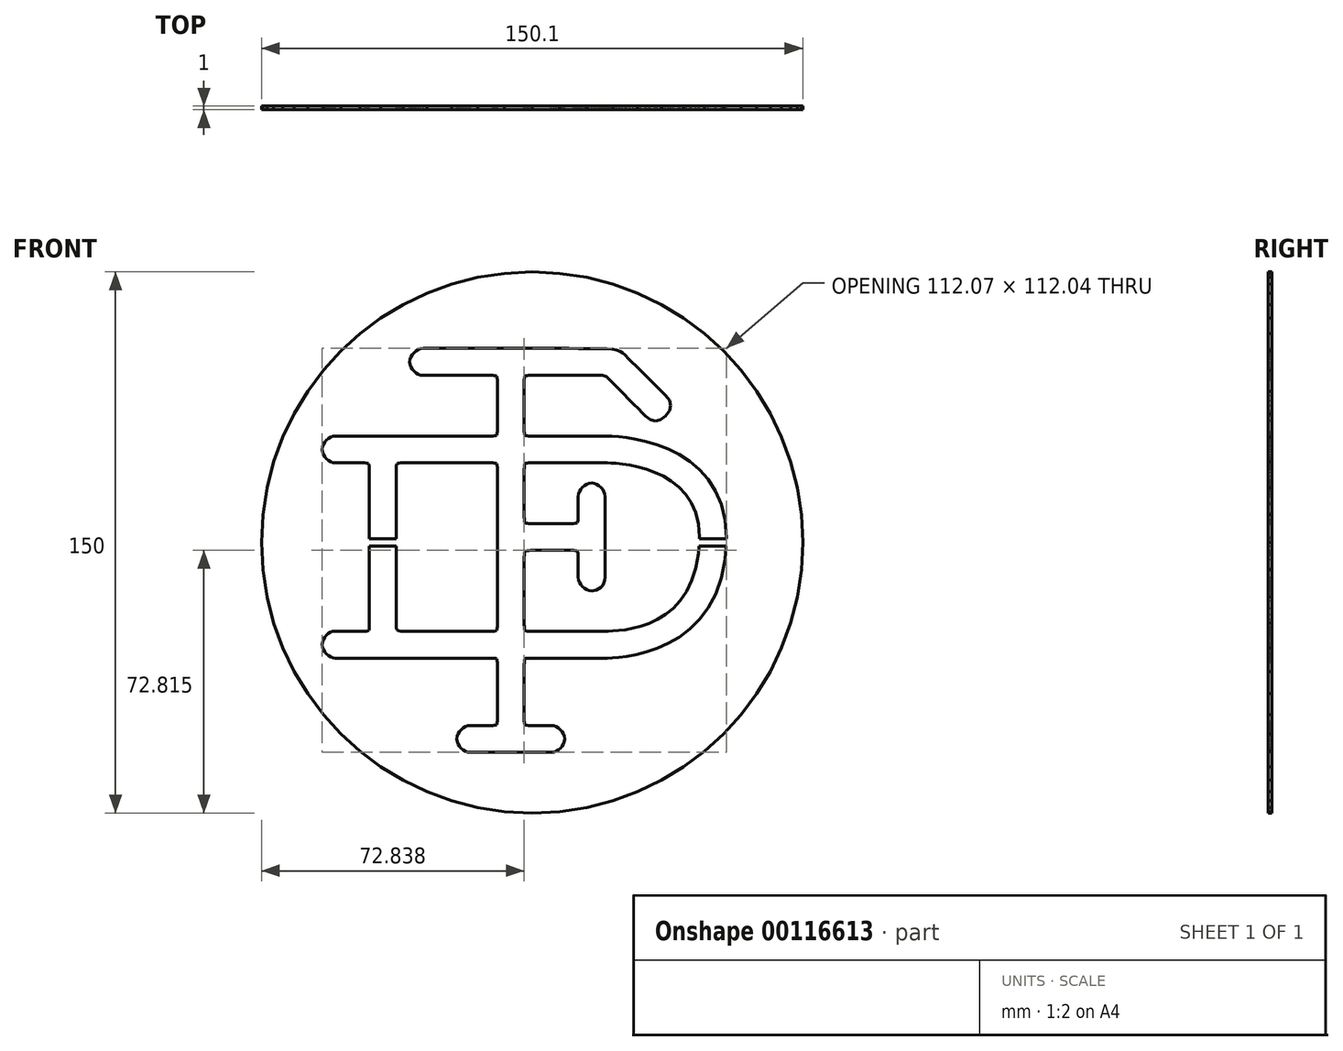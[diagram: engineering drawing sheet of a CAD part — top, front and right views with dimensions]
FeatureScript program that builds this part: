
annotation { "Feature Type Name" : "Feature", "Feature Type Description" : "" }
export const myFeature = defineFeature(function(context is Context, id is Id, definition is map)
    precondition{}
    {
        {
            var Q0;
            Q0=qCreatedBy(makeId("Front.planeOp"),FACE);
            var sketch = newSketch(context, id + "F0", { "sketchPlane" : qUnion([Q0])});
            skLineSegment(sketch, "E0", {"start": v(-30.25, 46.32) * mm, "end": v(-30.95, 46.4) * mm});
            skLineSegment(sketch, "E1", {"start": v(-30.95, 46.4) * mm, "end": v(-31.62, 46.64) * mm});
            skLineSegment(sketch, "E2", {"start": v(-31.62, 46.64) * mm, "end": v(-32.25, 47) * mm});
            skLineSegment(sketch, "E3", {"start": v(-32.25, 47) * mm, "end": v(-32.81, 47.49) * mm});
            skLineSegment(sketch, "E4", {"start": v(-32.81, 47.49) * mm, "end": v(-33.28, 48.05) * mm});
            skLineSegment(sketch, "E5", {"start": v(-33.28, 48.05) * mm, "end": v(-33.65, 48.68) * mm});
            skLineSegment(sketch, "E6", {"start": v(-33.65, 48.68) * mm, "end": v(-33.88, 49.35) * mm});
            skLineSegment(sketch, "E7", {"start": v(-33.88, 49.35) * mm, "end": v(-33.97, 50.05) * mm});
            skLineSegment(sketch, "E8", {"start": v(-33.97, 50.05) * mm, "end": v(-33.88, 50.75) * mm});
            skLineSegment(sketch, "E9", {"start": v(-33.88, 50.75) * mm, "end": v(-33.65, 51.43) * mm});
            skLineSegment(sketch, "E10", {"start": v(-33.65, 51.43) * mm, "end": v(-33.28, 52.07) * mm});
            skLineSegment(sketch, "E11", {"start": v(-33.28, 52.07) * mm, "end": v(-32.81, 52.64) * mm});
            skLineSegment(sketch, "E12", {"start": v(-32.81, 52.64) * mm, "end": v(-32.25, 53.13) * mm});
            skLineSegment(sketch, "E13", {"start": v(-32.25, 53.13) * mm, "end": v(-31.62, 53.5) * mm});
            skLineSegment(sketch, "E14", {"start": v(-31.62, 53.5) * mm, "end": v(-30.95, 53.75) * mm});
            skLineSegment(sketch, "E15", {"start": v(-30.95, 53.75) * mm, "end": v(-30.25, 53.84) * mm});
            skLineSegment(sketch, "E16", {"start": v(-30.25, 53.84) * mm, "end": v(-29.61, 53.84) * mm});
            skLineSegment(sketch, "E17", {"start": v(-29.61, 53.84) * mm, "end": v(-28.42, 53.83) * mm});
            skLineSegment(sketch, "E18", {"start": v(-28.42, 53.83) * mm, "end": v(-26.74, 53.83) * mm});
            skLineSegment(sketch, "E19", {"start": v(-26.74, 53.83) * mm, "end": v(-24.63, 53.83) * mm});
            skLineSegment(sketch, "E20", {"start": v(-24.63, 53.83) * mm, "end": v(-22.15, 53.82) * mm});
            skLineSegment(sketch, "E21", {"start": v(-22.15, 53.82) * mm, "end": v(-19.35, 53.82) * mm});
            skLineSegment(sketch, "E22", {"start": v(-19.35, 53.82) * mm, "end": v(-16.3, 53.82) * mm});
            skLineSegment(sketch, "E23", {"start": v(-16.3, 53.82) * mm, "end": v(-13.05, 53.81) * mm});
            skLineSegment(sketch, "E24", {"start": v(-13.05, 53.81) * mm, "end": v(-9.67, 53.8) * mm});
            skLineSegment(sketch, "E25", {"start": v(-9.67, 53.8) * mm, "end": v(-6.2, 53.8) * mm});
            skLineSegment(sketch, "E26", {"start": v(-6.2, 53.8) * mm, "end": v(-2.73, 53.8) * mm});
            skLineSegment(sketch, "E27", {"start": v(-2.73, 53.8) * mm, "end": v(0.71, 53.8) * mm});
            skLineSegment(sketch, "E28", {"start": v(0.71, 53.8) * mm, "end": v(4.05, 53.8) * mm});
            skLineSegment(sketch, "E29", {"start": v(4.05, 53.8) * mm, "end": v(7.24, 53.79) * mm});
            skLineSegment(sketch, "E30", {"start": v(7.24, 53.79) * mm, "end": v(10.2, 53.79) * mm});
            skLineSegment(sketch, "E31", {"start": v(10.2, 53.79) * mm, "end": v(12.9, 53.79) * mm});
            skLineSegment(sketch, "E32", {"start": v(12.9, 53.79) * mm, "end": v(16.15, 53.78) * mm});
            skLineSegment(sketch, "E33", {"start": v(16.15, 53.78) * mm, "end": v(18.72, 53.76) * mm});
            skLineSegment(sketch, "E34", {"start": v(18.72, 53.76) * mm, "end": v(20.72, 53.7) * mm});
            skLineSegment(sketch, "E35", {"start": v(20.72, 53.7) * mm, "end": v(22.25, 53.57) * mm});
            skLineSegment(sketch, "E36", {"start": v(22.25, 53.57) * mm, "end": v(23.42, 53.35) * mm});
            skLineSegment(sketch, "E37", {"start": v(23.42, 53.35) * mm, "end": v(24.34, 53.01) * mm});
            skLineSegment(sketch, "E38", {"start": v(24.34, 53.01) * mm, "end": v(25.1, 52.55) * mm});
            skLineSegment(sketch, "E39", {"start": v(25.1, 52.55) * mm, "end": v(25.8, 51.92) * mm});
            skLineSegment(sketch, "E40", {"start": v(25.8, 51.92) * mm, "end": v(26.74, 50.98) * mm});
            skLineSegment(sketch, "E41", {"start": v(26.74, 50.98) * mm, "end": v(28.08, 49.64) * mm});
            skLineSegment(sketch, "E42", {"start": v(28.08, 49.64) * mm, "end": v(29.68, 48.05) * mm});
            skLineSegment(sketch, "E43", {"start": v(29.68, 48.05) * mm, "end": v(31.4, 46.32) * mm});
            skLineSegment(sketch, "E44", {"start": v(31.4, 46.32) * mm, "end": v(33.14, 44.6) * mm});
            skLineSegment(sketch, "E45", {"start": v(33.14, 44.6) * mm, "end": v(34.73, 43) * mm});
            skLineSegment(sketch, "E46", {"start": v(34.73, 43) * mm, "end": v(36.07, 41.66) * mm});
            skLineSegment(sketch, "E47", {"start": v(36.07, 41.66) * mm, "end": v(37, 40.72) * mm});
            skLineSegment(sketch, "E48", {"start": v(37, 40.72) * mm, "end": v(38.06, 39.32) * mm});
            skLineSegment(sketch, "E49", {"start": v(38.06, 39.32) * mm, "end": v(38.41, 37.92) * mm});
            skLineSegment(sketch, "E50", {"start": v(38.41, 37.92) * mm, "end": v(38.06, 36.52) * mm});
            skLineSegment(sketch, "E51", {"start": v(38.06, 36.52) * mm, "end": v(37, 35.12) * mm});
            skLineSegment(sketch, "E52", {"start": v(37, 35.12) * mm, "end": v(35.6, 34.07) * mm});
            skLineSegment(sketch, "E53", {"start": v(35.6, 34.07) * mm, "end": v(34.2, 33.72) * mm});
            skLineSegment(sketch, "E54", {"start": v(34.2, 33.72) * mm, "end": v(32.8, 34.07) * mm});
            skLineSegment(sketch, "E55", {"start": v(32.8, 34.07) * mm, "end": v(31.4, 35.12) * mm});
            skLineSegment(sketch, "E56", {"start": v(31.4, 35.12) * mm, "end": v(30.55, 35.98) * mm});
            skLineSegment(sketch, "E57", {"start": v(30.55, 35.98) * mm, "end": v(29.42, 37.11) * mm});
            skLineSegment(sketch, "E58", {"start": v(29.42, 37.11) * mm, "end": v(28.13, 38.42) * mm});
            skLineSegment(sketch, "E59", {"start": v(28.13, 38.42) * mm, "end": v(26.74, 39.81) * mm});
            skLineSegment(sketch, "E60", {"start": v(26.74, 39.81) * mm, "end": v(25.35, 41.2) * mm});
            skLineSegment(sketch, "E61", {"start": v(25.35, 41.2) * mm, "end": v(24.05, 42.51) * mm});
            skLineSegment(sketch, "E62", {"start": v(24.05, 42.51) * mm, "end": v(22.93, 43.64) * mm});
            skLineSegment(sketch, "E63", {"start": v(22.93, 43.64) * mm, "end": v(22.07, 44.5) * mm});
            skLineSegment(sketch, "E64", {"start": v(22.07, 44.5) * mm, "end": v(21.45, 45.12) * mm});
            skLineSegment(sketch, "E65", {"start": v(21.45, 45.12) * mm, "end": v(20.96, 45.58) * mm});
            skLineSegment(sketch, "E66", {"start": v(20.96, 45.58) * mm, "end": v(20.56, 45.92) * mm});
            skLineSegment(sketch, "E67", {"start": v(20.56, 45.92) * mm, "end": v(20.2, 46.14) * mm});
            skLineSegment(sketch, "E68", {"start": v(20.2, 46.14) * mm, "end": v(19.84, 46.28) * mm});
            skLineSegment(sketch, "E69", {"start": v(19.84, 46.28) * mm, "end": v(19.43, 46.34) * mm});
            skLineSegment(sketch, "E70", {"start": v(19.43, 46.34) * mm, "end": v(18.94, 46.37) * mm});
            skLineSegment(sketch, "E71", {"start": v(18.94, 46.37) * mm, "end": v(18.3, 46.37) * mm});
            skLineSegment(sketch, "E72", {"start": v(18.3, 46.37) * mm, "end": v(17.02, 46.37) * mm});
            skLineSegment(sketch, "E73", {"start": v(17.02, 46.37) * mm, "end": v(14.8, 46.37) * mm});
            skLineSegment(sketch, "E74", {"start": v(14.8, 46.37) * mm, "end": v(11.95, 46.36) * mm});
            skLineSegment(sketch, "E75", {"start": v(11.95, 46.36) * mm, "end": v(8.8, 46.35) * mm});
            skLineSegment(sketch, "E76", {"start": v(8.8, 46.35) * mm, "end": v(5.66, 46.34) * mm});
            skLineSegment(sketch, "E77", {"start": v(5.66, 46.34) * mm, "end": v(2.88, 46.33) * mm});
            skLineSegment(sketch, "E78", {"start": v(2.88, 46.33) * mm, "end": v(0.76, 46.32) * mm});
            skLineSegment(sketch, "E79", {"start": v(0.76, 46.32) * mm, "end": v(-0.37, 46.32) * mm});
            skLineSegment(sketch, "E80", {"start": v(-0.37, 46.32) * mm, "end": v(-0.98, 46.32) * mm});
            skLineSegment(sketch, "E81", {"start": v(-0.98, 46.32) * mm, "end": v(-1.44, 46.3) * mm});
            skLineSegment(sketch, "E82", {"start": v(-1.44, 46.3) * mm, "end": v(-1.76, 46.22) * mm});
            skLineSegment(sketch, "E83", {"start": v(-1.76, 46.22) * mm, "end": v(-1.98, 46.09) * mm});
            skLineSegment(sketch, "E84", {"start": v(-1.98, 46.09) * mm, "end": v(-2.12, 45.87) * mm});
            skLineSegment(sketch, "E85", {"start": v(-2.12, 45.87) * mm, "end": v(-2.18, 45.54) * mm});
            skLineSegment(sketch, "E86", {"start": v(-2.18, 45.54) * mm, "end": v(-2.2, 45.09) * mm});
            skLineSegment(sketch, "E87", {"start": v(-2.2, 45.09) * mm, "end": v(-2.21, 44.48) * mm});
            skLineSegment(sketch, "E88", {"start": v(-2.21, 44.48) * mm, "end": v(-2.21, 43.46) * mm});
            skLineSegment(sketch, "E89", {"start": v(-2.21, 43.46) * mm, "end": v(-2.21, 41.91) * mm});
            skLineSegment(sketch, "E90", {"start": v(-2.21, 41.91) * mm, "end": v(-2.21, 40.02) * mm});
            skLineSegment(sketch, "E91", {"start": v(-2.21, 40.02) * mm, "end": v(-2.21, 37.94) * mm});
            skLineSegment(sketch, "E92", {"start": v(-2.21, 37.94) * mm, "end": v(-2.21, 35.87) * mm});
            skLineSegment(sketch, "E93", {"start": v(-2.21, 35.87) * mm, "end": v(-2.21, 33.98) * mm});
            skLineSegment(sketch, "E94", {"start": v(-2.21, 33.98) * mm, "end": v(-2.21, 32.43) * mm});
            skLineSegment(sketch, "E95", {"start": v(-2.21, 32.43) * mm, "end": v(-2.21, 31.41) * mm});
            skLineSegment(sketch, "E96", {"start": v(-2.21, 31.41) * mm, "end": v(-2.2, 30.79) * mm});
            skLineSegment(sketch, "E97", {"start": v(-2.2, 30.79) * mm, "end": v(-2.18, 30.32) * mm});
            skLineSegment(sketch, "E98", {"start": v(-2.18, 30.32) * mm, "end": v(-2.12, 29.98) * mm});
            skLineSegment(sketch, "E99", {"start": v(-2.12, 29.98) * mm, "end": v(-1.98, 29.76) * mm});
            skLineSegment(sketch, "E100", {"start": v(-1.98, 29.76) * mm, "end": v(-1.76, 29.62) * mm});
            skLineSegment(sketch, "E101", {"start": v(-1.76, 29.62) * mm, "end": v(-1.44, 29.55) * mm});
            skLineSegment(sketch, "E102", {"start": v(-1.44, 29.55) * mm, "end": v(-0.98, 29.52) * mm});
            skLineSegment(sketch, "E103", {"start": v(-0.98, 29.52) * mm, "end": v(-0.37, 29.52) * mm});
            skLineSegment(sketch, "E104", {"start": v(-0.37, 29.52) * mm, "end": v(0.97, 29.52) * mm});
            skLineSegment(sketch, "E105", {"start": v(0.97, 29.52) * mm, "end": v(3.37, 29.52) * mm});
            skLineSegment(sketch, "E106", {"start": v(3.37, 29.52) * mm, "end": v(6.46, 29.52) * mm});
            skLineSegment(sketch, "E107", {"start": v(6.46, 29.52) * mm, "end": v(9.9, 29.52) * mm});
            skLineSegment(sketch, "E108", {"start": v(9.9, 29.52) * mm, "end": v(13.35, 29.52) * mm});
            skLineSegment(sketch, "E109", {"start": v(13.35, 29.52) * mm, "end": v(16.45, 29.52) * mm});
            skLineSegment(sketch, "E110", {"start": v(16.45, 29.52) * mm, "end": v(18.85, 29.52) * mm});
            skLineSegment(sketch, "E111", {"start": v(18.85, 29.52) * mm, "end": v(20.2, 29.52) * mm});
            skLineSegment(sketch, "E112", {"start": v(20.2, 29.52) * mm, "end": v(20.88, 29.5) * mm});
            skLineSegment(sketch, "E113", {"start": v(20.88, 29.5) * mm, "end": v(22.17, 29.45) * mm});
            skLineSegment(sketch, "E114", {"start": v(22.17, 29.45) * mm, "end": v(23.99, 29.31) * mm});
            skLineSegment(sketch, "E115", {"start": v(23.99, 29.31) * mm, "end": v(26.23, 29.04) * mm});
            skLineSegment(sketch, "E116", {"start": v(26.23, 29.04) * mm, "end": v(28.8, 28.6) * mm});
            skLineSegment(sketch, "E117", {"start": v(28.8, 28.6) * mm, "end": v(31.64, 27.96) * mm});
            skLineSegment(sketch, "E118", {"start": v(31.64, 27.96) * mm, "end": v(34.63, 27.07) * mm});
            skLineSegment(sketch, "E119", {"start": v(34.63, 27.07) * mm, "end": v(37.7, 25.9) * mm});
            skLineSegment(sketch, "E120", {"start": v(37.7, 25.9) * mm, "end": v(40.73, 24.39) * mm});
            skLineSegment(sketch, "E121", {"start": v(40.73, 24.39) * mm, "end": v(43.66, 22.51) * mm});
            skLineSegment(sketch, "E122", {"start": v(43.66, 22.51) * mm, "end": v(46.38, 20.23) * mm});
            skLineSegment(sketch, "E123", {"start": v(46.38, 20.23) * mm, "end": v(48.81, 17.5) * mm});
            skLineSegment(sketch, "E124", {"start": v(48.81, 17.5) * mm, "end": v(50.87, 14.27) * mm});
            skLineSegment(sketch, "E125", {"start": v(50.87, 14.27) * mm, "end": v(52.44, 10.52) * mm});
            skLineSegment(sketch, "E126", {"start": v(52.44, 10.52) * mm, "end": v(53.46, 6.2) * mm});
            skLineSegment(sketch, "E127", {"start": v(53.46, 6.2) * mm, "end": v(53.82, 1.27) * mm});
            skLineSegment(sketch, "E128", {"start": v(53.82, 1.27) * mm, "end": v(53.47, -4.64) * mm});
            skLineSegment(sketch, "E129", {"start": v(53.47, -4.64) * mm, "end": v(52.46, -9.8) * mm});
            skLineSegment(sketch, "E130", {"start": v(52.46, -9.8) * mm, "end": v(50.89, -14.28) * mm});
            skLineSegment(sketch, "E131", {"start": v(50.89, -14.28) * mm, "end": v(48.84, -18.11) * mm});
            skLineSegment(sketch, "E132", {"start": v(48.84, -18.11) * mm, "end": v(46.41, -21.35) * mm});
            skLineSegment(sketch, "E133", {"start": v(46.41, -21.35) * mm, "end": v(43.68, -24.04) * mm});
            skLineSegment(sketch, "E134", {"start": v(43.68, -24.04) * mm, "end": v(40.76, -26.24) * mm});
            skLineSegment(sketch, "E135", {"start": v(40.76, -26.24) * mm, "end": v(37.72, -28) * mm});
            skLineSegment(sketch, "E136", {"start": v(37.72, -28) * mm, "end": v(34.65, -29.36) * mm});
            skLineSegment(sketch, "E137", {"start": v(34.65, -29.36) * mm, "end": v(31.66, -30.38) * mm});
            skLineSegment(sketch, "E138", {"start": v(31.66, -30.38) * mm, "end": v(28.82, -31.1) * mm});
            skLineSegment(sketch, "E139", {"start": v(28.82, -31.1) * mm, "end": v(26.24, -31.59) * mm});
            skLineSegment(sketch, "E140", {"start": v(26.24, -31.59) * mm, "end": v(24, -31.87) * mm});
            skLineSegment(sketch, "E141", {"start": v(24, -31.87) * mm, "end": v(22.18, -32.02) * mm});
            skLineSegment(sketch, "E142", {"start": v(22.18, -32.02) * mm, "end": v(20.88, -32.07) * mm});
            skLineSegment(sketch, "E143", {"start": v(20.88, -32.07) * mm, "end": v(20.2, -32.07) * mm});
            skLineSegment(sketch, "E144", {"start": v(20.2, -32.07) * mm, "end": v(18.64, -32.07) * mm});
            skLineSegment(sketch, "E145", {"start": v(18.64, -32.07) * mm, "end": v(16.14, -32.07) * mm});
            skLineSegment(sketch, "E146", {"start": v(16.14, -32.07) * mm, "end": v(13.02, -32.07) * mm});
            skLineSegment(sketch, "E147", {"start": v(13.02, -32.07) * mm, "end": v(9.62, -32.07) * mm});
            skLineSegment(sketch, "E148", {"start": v(9.62, -32.07) * mm, "end": v(6.26, -32.07) * mm});
            skLineSegment(sketch, "E149", {"start": v(6.26, -32.07) * mm, "end": v(3.26, -32.07) * mm});
            skLineSegment(sketch, "E150", {"start": v(3.26, -32.07) * mm, "end": v(0.94, -32.07) * mm});
            skLineSegment(sketch, "E151", {"start": v(0.94, -32.07) * mm, "end": v(-0.38, -32.07) * mm});
            skLineSegment(sketch, "E152", {"start": v(-0.38, -32.07) * mm, "end": v(-0.98, -32.07) * mm});
            skLineSegment(sketch, "E153", {"start": v(-0.98, -32.07) * mm, "end": v(-1.44, -32.1) * mm});
            skLineSegment(sketch, "E154", {"start": v(-1.44, -32.1) * mm, "end": v(-1.76, -32.16) * mm});
            skLineSegment(sketch, "E155", {"start": v(-1.76, -32.16) * mm, "end": v(-1.98, -32.3) * mm});
            skLineSegment(sketch, "E156", {"start": v(-1.98, -32.3) * mm, "end": v(-2.11, -32.5) * mm});
            skLineSegment(sketch, "E157", {"start": v(-2.11, -32.5) * mm, "end": v(-2.18, -32.84) * mm});
            skLineSegment(sketch, "E158", {"start": v(-2.18, -32.84) * mm, "end": v(-2.2, -33.3) * mm});
            skLineSegment(sketch, "E159", {"start": v(-2.2, -33.3) * mm, "end": v(-2.21, -33.91) * mm});
            skLineSegment(sketch, "E160", {"start": v(-2.21, -33.91) * mm, "end": v(-2.21, -35.04) * mm});
            skLineSegment(sketch, "E161", {"start": v(-2.21, -35.04) * mm, "end": v(-2.21, -36.88) * mm});
            skLineSegment(sketch, "E162", {"start": v(-2.21, -36.88) * mm, "end": v(-2.21, -39.17) * mm});
            skLineSegment(sketch, "E163", {"start": v(-2.21, -39.17) * mm, "end": v(-2.21, -41.66) * mm});
            skLineSegment(sketch, "E164", {"start": v(-2.21, -41.66) * mm, "end": v(-2.21, -44.13) * mm});
            skLineSegment(sketch, "E165", {"start": v(-2.21, -44.13) * mm, "end": v(-2.21, -46.3) * mm});
            skLineSegment(sketch, "E166", {"start": v(-2.21, -46.3) * mm, "end": v(-2.21, -47.96) * mm});
            skLineSegment(sketch, "E167", {"start": v(-2.21, -47.96) * mm, "end": v(-2.21, -48.84) * mm});
            skLineSegment(sketch, "E168", {"start": v(-2.21, -48.84) * mm, "end": v(-2.2, -49.47) * mm});
            skLineSegment(sketch, "E169", {"start": v(-2.2, -49.47) * mm, "end": v(-2.19, -49.94) * mm});
            skLineSegment(sketch, "E170", {"start": v(-2.19, -49.94) * mm, "end": v(-2.12, -50.27) * mm});
            skLineSegment(sketch, "E171", {"start": v(-2.12, -50.27) * mm, "end": v(-2, -50.5) * mm});
            skLineSegment(sketch, "E172", {"start": v(-2, -50.5) * mm, "end": v(-1.78, -50.64) * mm});
            skLineSegment(sketch, "E173", {"start": v(-1.78, -50.64) * mm, "end": v(-1.45, -50.7) * mm});
            skLineSegment(sketch, "E174", {"start": v(-1.45, -50.7) * mm, "end": v(-1, -50.73) * mm});
            skLineSegment(sketch, "E175", {"start": v(-1, -50.73) * mm, "end": v(-0.38, -50.74) * mm});
            skLineSegment(sketch, "E176", {"start": v(-0.38, -50.74) * mm, "end": v(5.23, -50.74) * mm});
            skLineSegment(sketch, "E177", {"start": v(5.23, -50.74) * mm, "end": v(5.93, -50.82) * mm});
            skLineSegment(sketch, "E178", {"start": v(5.93, -50.82) * mm, "end": v(6.6, -51.06) * mm});
            skLineSegment(sketch, "E179", {"start": v(6.6, -51.06) * mm, "end": v(7.24, -51.43) * mm});
            skLineSegment(sketch, "E180", {"start": v(7.24, -51.43) * mm, "end": v(7.81, -51.9) * mm});
            skLineSegment(sketch, "E181", {"start": v(7.81, -51.9) * mm, "end": v(8.3, -52.47) * mm});
            skLineSegment(sketch, "E182", {"start": v(8.3, -52.47) * mm, "end": v(8.67, -53.1) * mm});
            skLineSegment(sketch, "E183", {"start": v(8.67, -53.1) * mm, "end": v(8.9, -53.77) * mm});
            skLineSegment(sketch, "E184", {"start": v(8.9, -53.77) * mm, "end": v(9, -54.47) * mm});
            skLineSegment(sketch, "E185", {"start": v(9, -54.47) * mm, "end": v(8.9, -55.17) * mm});
            skLineSegment(sketch, "E186", {"start": v(8.9, -55.17) * mm, "end": v(8.67, -55.84) * mm});
            skLineSegment(sketch, "E187", {"start": v(8.67, -55.84) * mm, "end": v(8.3, -56.47) * mm});
            skLineSegment(sketch, "E188", {"start": v(8.3, -56.47) * mm, "end": v(7.83, -57.04) * mm});
            skLineSegment(sketch, "E189", {"start": v(7.83, -57.04) * mm, "end": v(7.26, -57.52) * mm});
            skLineSegment(sketch, "E190", {"start": v(7.26, -57.52) * mm, "end": v(6.63, -57.88) * mm});
            skLineSegment(sketch, "E191", {"start": v(6.63, -57.88) * mm, "end": v(5.95, -58.12) * mm});
            skLineSegment(sketch, "E192", {"start": v(5.95, -58.12) * mm, "end": v(5.26, -58.2) * mm});
            skLineSegment(sketch, "E193", {"start": v(5.26, -58.2) * mm, "end": v(3.82, -58.2) * mm});
            skLineSegment(sketch, "E194", {"start": v(3.82, -58.2) * mm, "end": v(1.2, -58.2) * mm});
            skLineSegment(sketch, "E195", {"start": v(1.2, -58.2) * mm, "end": v(-2.24, -58.2) * mm});
            skLineSegment(sketch, "E196", {"start": v(-2.24, -58.2) * mm, "end": v(-6.06, -58.2) * mm});
            skLineSegment(sketch, "E197", {"start": v(-6.06, -58.2) * mm, "end": v(-9.86, -58.2) * mm});
            skLineSegment(sketch, "E198", {"start": v(-9.86, -58.2) * mm, "end": v(-13.25, -58.2) * mm});
            skLineSegment(sketch, "E199", {"start": v(-13.25, -58.2) * mm, "end": v(-15.82, -58.2) * mm});
            skLineSegment(sketch, "E200", {"start": v(-15.82, -58.2) * mm, "end": v(-17.16, -58.2) * mm});
            skLineSegment(sketch, "E201", {"start": v(-17.16, -58.2) * mm, "end": v(-17.86, -58.12) * mm});
            skLineSegment(sketch, "E202", {"start": v(-17.86, -58.12) * mm, "end": v(-18.53, -57.88) * mm});
            skLineSegment(sketch, "E203", {"start": v(-18.53, -57.88) * mm, "end": v(-19.17, -57.52) * mm});
            skLineSegment(sketch, "E204", {"start": v(-19.17, -57.52) * mm, "end": v(-19.74, -57.04) * mm});
            skLineSegment(sketch, "E205", {"start": v(-19.74, -57.04) * mm, "end": v(-20.21, -56.47) * mm});
            skLineSegment(sketch, "E206", {"start": v(-20.21, -56.47) * mm, "end": v(-20.58, -55.84) * mm});
            skLineSegment(sketch, "E207", {"start": v(-20.58, -55.84) * mm, "end": v(-20.81, -55.17) * mm});
            skLineSegment(sketch, "E208", {"start": v(-20.81, -55.17) * mm, "end": v(-20.89, -54.47) * mm});
            skLineSegment(sketch, "E209", {"start": v(-20.89, -54.47) * mm, "end": v(-20.8, -53.77) * mm});
            skLineSegment(sketch, "E210", {"start": v(-20.8, -53.77) * mm, "end": v(-20.56, -53.1) * mm});
            skLineSegment(sketch, "E211", {"start": v(-20.56, -53.1) * mm, "end": v(-20.2, -52.47) * mm});
            skLineSegment(sketch, "E212", {"start": v(-20.2, -52.47) * mm, "end": v(-19.73, -51.9) * mm});
            skLineSegment(sketch, "E213", {"start": v(-19.73, -51.9) * mm, "end": v(-19.18, -51.43) * mm});
            skLineSegment(sketch, "E214", {"start": v(-19.18, -51.43) * mm, "end": v(-18.56, -51.06) * mm});
            skLineSegment(sketch, "E215", {"start": v(-18.56, -51.06) * mm, "end": v(-17.9, -50.82) * mm});
            skLineSegment(sketch, "E216", {"start": v(-17.9, -50.82) * mm, "end": v(-17.21, -50.74) * mm});
            skLineSegment(sketch, "E217", {"start": v(-17.21, -50.74) * mm, "end": v(-15.66, -50.74) * mm});
            skLineSegment(sketch, "E218", {"start": v(-15.66, -50.74) * mm, "end": v(-14.01, -50.74) * mm});
            skLineSegment(sketch, "E219", {"start": v(-14.01, -50.74) * mm, "end": v(-12.56, -50.74) * mm});
            skLineSegment(sketch, "E220", {"start": v(-12.56, -50.74) * mm, "end": v(-11.55, -50.74) * mm});
            skLineSegment(sketch, "E221", {"start": v(-11.55, -50.74) * mm, "end": v(-10.94, -50.73) * mm});
            skLineSegment(sketch, "E222", {"start": v(-10.94, -50.73) * mm, "end": v(-10.47, -50.7) * mm});
            skLineSegment(sketch, "E223", {"start": v(-10.47, -50.7) * mm, "end": v(-10.14, -50.64) * mm});
            skLineSegment(sketch, "E224", {"start": v(-10.14, -50.64) * mm, "end": v(-9.92, -50.5) * mm});
            skLineSegment(sketch, "E225", {"start": v(-9.92, -50.5) * mm, "end": v(-9.78, -50.28) * mm});
            skLineSegment(sketch, "E226", {"start": v(-9.78, -50.28) * mm, "end": v(-9.71, -49.95) * mm});
            skLineSegment(sketch, "E227", {"start": v(-9.71, -49.95) * mm, "end": v(-9.69, -49.48) * mm});
            skLineSegment(sketch, "E228", {"start": v(-9.69, -49.48) * mm, "end": v(-9.68, -48.87) * mm});
            skLineSegment(sketch, "E229", {"start": v(-9.68, -48.87) * mm, "end": v(-9.68, -47.74) * mm});
            skLineSegment(sketch, "E230", {"start": v(-9.68, -47.74) * mm, "end": v(-9.68, -45.93) * mm});
            skLineSegment(sketch, "E231", {"start": v(-9.68, -45.93) * mm, "end": v(-9.68, -43.67) * mm});
            skLineSegment(sketch, "E232", {"start": v(-9.68, -43.67) * mm, "end": v(-9.68, -41.2) * mm});
            skLineSegment(sketch, "E233", {"start": v(-9.68, -41.2) * mm, "end": v(-9.68, -38.74) * mm});
            skLineSegment(sketch, "E234", {"start": v(-9.68, -38.74) * mm, "end": v(-9.68, -36.56) * mm});
            skLineSegment(sketch, "E235", {"start": v(-9.68, -36.56) * mm, "end": v(-9.68, -34.88) * mm});
            skLineSegment(sketch, "E236", {"start": v(-9.68, -34.88) * mm, "end": v(-9.68, -33.94) * mm});
            skLineSegment(sketch, "E237", {"start": v(-9.68, -33.94) * mm, "end": v(-9.69, -33.32) * mm});
            skLineSegment(sketch, "E238", {"start": v(-9.69, -33.32) * mm, "end": v(-9.71, -32.86) * mm});
            skLineSegment(sketch, "E239", {"start": v(-9.71, -32.86) * mm, "end": v(-9.78, -32.53) * mm});
            skLineSegment(sketch, "E240", {"start": v(-9.78, -32.53) * mm, "end": v(-9.92, -32.3) * mm});
            skLineSegment(sketch, "E241", {"start": v(-9.92, -32.3) * mm, "end": v(-10.14, -32.17) * mm});
            skLineSegment(sketch, "E242", {"start": v(-10.14, -32.17) * mm, "end": v(-10.47, -32.1) * mm});
            skLineSegment(sketch, "E243", {"start": v(-10.47, -32.1) * mm, "end": v(-10.94, -32.08) * mm});
            skLineSegment(sketch, "E244", {"start": v(-10.94, -32.08) * mm, "end": v(-11.55, -32.07) * mm});
            skLineSegment(sketch, "E245", {"start": v(-11.55, -32.07) * mm, "end": v(-12.32, -32.07) * mm});
            skLineSegment(sketch, "E246", {"start": v(-12.32, -32.07) * mm, "end": v(-13.86, -32.07) * mm});
            skLineSegment(sketch, "E247", {"start": v(-13.86, -32.07) * mm, "end": v(-16.05, -32.07) * mm});
            skLineSegment(sketch, "E248", {"start": v(-16.05, -32.07) * mm, "end": v(-18.8, -32.07) * mm});
            skLineSegment(sketch, "E249", {"start": v(-18.8, -32.07) * mm, "end": v(-21.97, -32.07) * mm});
            skLineSegment(sketch, "E250", {"start": v(-21.97, -32.07) * mm, "end": v(-25.48, -32.07) * mm});
            skLineSegment(sketch, "E251", {"start": v(-25.48, -32.07) * mm, "end": v(-29.2, -32.07) * mm});
            skLineSegment(sketch, "E252", {"start": v(-29.2, -32.07) * mm, "end": v(-33.04, -32.07) * mm});
            skLineSegment(sketch, "E253", {"start": v(-33.04, -32.07) * mm, "end": v(-36.88, -32.07) * mm});
            skLineSegment(sketch, "E254", {"start": v(-36.88, -32.07) * mm, "end": v(-40.6, -32.07) * mm});
            skLineSegment(sketch, "E255", {"start": v(-40.6, -32.07) * mm, "end": v(-44.12, -32.07) * mm});
            skLineSegment(sketch, "E256", {"start": v(-44.12, -32.07) * mm, "end": v(-47.3, -32.07) * mm});
            skLineSegment(sketch, "E257", {"start": v(-47.3, -32.07) * mm, "end": v(-50.04, -32.07) * mm});
            skLineSegment(sketch, "E258", {"start": v(-50.04, -32.07) * mm, "end": v(-52.23, -32.07) * mm});
            skLineSegment(sketch, "E259", {"start": v(-52.23, -32.07) * mm, "end": v(-53.77, -32.07) * mm});
            skLineSegment(sketch, "E260", {"start": v(-53.77, -32.07) * mm, "end": v(-54.54, -32.07) * mm});
            skLineSegment(sketch, "E261", {"start": v(-54.54, -32.07) * mm, "end": v(-55.23, -31.99) * mm});
            skLineSegment(sketch, "E262", {"start": v(-55.23, -31.99) * mm, "end": v(-55.9, -31.75) * mm});
            skLineSegment(sketch, "E263", {"start": v(-55.9, -31.75) * mm, "end": v(-56.53, -31.38) * mm});
            skLineSegment(sketch, "E264", {"start": v(-56.53, -31.38) * mm, "end": v(-57.1, -30.9) * mm});
            skLineSegment(sketch, "E265", {"start": v(-57.1, -30.9) * mm, "end": v(-57.56, -30.34) * mm});
            skLineSegment(sketch, "E266", {"start": v(-57.56, -30.34) * mm, "end": v(-57.93, -29.7) * mm});
            skLineSegment(sketch, "E267", {"start": v(-57.93, -29.7) * mm, "end": v(-58.16, -29.04) * mm});
            skLineSegment(sketch, "E268", {"start": v(-58.16, -29.04) * mm, "end": v(-58.24, -28.34) * mm});
            skLineSegment(sketch, "E269", {"start": v(-58.24, -28.34) * mm, "end": v(-58.16, -27.64) * mm});
            skLineSegment(sketch, "E270", {"start": v(-58.16, -27.64) * mm, "end": v(-57.93, -26.97) * mm});
            skLineSegment(sketch, "E271", {"start": v(-57.93, -26.97) * mm, "end": v(-57.57, -26.34) * mm});
            skLineSegment(sketch, "E272", {"start": v(-57.57, -26.34) * mm, "end": v(-57.11, -25.77) * mm});
            skLineSegment(sketch, "E273", {"start": v(-57.11, -25.77) * mm, "end": v(-56.57, -25.3) * mm});
            skLineSegment(sketch, "E274", {"start": v(-56.57, -25.3) * mm, "end": v(-55.97, -24.93) * mm});
            skLineSegment(sketch, "E275", {"start": v(-55.97, -24.93) * mm, "end": v(-55.34, -24.69) * mm});
            skLineSegment(sketch, "E276", {"start": v(-55.34, -24.69) * mm, "end": v(-54.7, -24.6) * mm});
            skLineSegment(sketch, "E277", {"start": v(-54.7, -24.6) * mm, "end": v(-52.89, -24.6) * mm});
            skLineSegment(sketch, "E278", {"start": v(-52.89, -24.6) * mm, "end": v(-50.76, -24.6) * mm});
            skLineSegment(sketch, "E279", {"start": v(-50.76, -24.6) * mm, "end": v(-48.7, -24.6) * mm});
            skLineSegment(sketch, "E280", {"start": v(-48.7, -24.6) * mm, "end": v(-47.07, -24.6) * mm});
            skLineSegment(sketch, "E281", {"start": v(-47.07, -24.6) * mm, "end": v(-46.4, -24.6) * mm});
            skLineSegment(sketch, "E282", {"start": v(-46.4, -24.6) * mm, "end": v(-45.9, -24.58) * mm});
            skLineSegment(sketch, "E283", {"start": v(-45.9, -24.58) * mm, "end": v(-45.57, -24.5) * mm});
            skLineSegment(sketch, "E284", {"start": v(-45.57, -24.5) * mm, "end": v(-45.35, -24.37) * mm});
            skLineSegment(sketch, "E285", {"start": v(-45.35, -24.37) * mm, "end": v(-45.23, -24.14) * mm});
            skLineSegment(sketch, "E286", {"start": v(-45.23, -24.14) * mm, "end": v(-45.18, -23.8) * mm});
            skLineSegment(sketch, "E287", {"start": v(-45.18, -23.8) * mm, "end": v(-45.17, -23.34) * mm});
            skLineSegment(sketch, "E288", {"start": v(-45.17, -23.34) * mm, "end": v(-45.17, -22.71) * mm});
            skLineSegment(sketch, "E289", {"start": v(-45.17, -22.71) * mm, "end": v(-45.17, -21.94) * mm});
            skLineSegment(sketch, "E290", {"start": v(-45.17, -21.94) * mm, "end": v(-45.17, -20.4) * mm});
            skLineSegment(sketch, "E291", {"start": v(-45.17, -20.4) * mm, "end": v(-45.17, -18.22) * mm});
            skLineSegment(sketch, "E292", {"start": v(-45.17, -18.22) * mm, "end": v(-45.17, -15.48) * mm});
            skLineSegment(sketch, "E293", {"start": v(-45.17, -15.48) * mm, "end": v(-45.17, -12.3) * mm});
            skLineSegment(sketch, "E294", {"start": v(-45.17, -12.3) * mm, "end": v(-45.17, -8.8) * mm});
            skLineSegment(sketch, "E295", {"start": v(-45.17, -8.8) * mm, "end": v(-45.17, -5.08) * mm});
            skLineSegment(sketch, "E296", {"start": v(-45.17, -5.08) * mm, "end": v(-45.17, -1.25) * mm});
            skLineSegment(sketch, "E297", {"start": v(-45.17, -1.25) * mm, "end": v(-45.17, 2.58) * mm});
            skLineSegment(sketch, "E298", {"start": v(-45.17, 2.58) * mm, "end": v(-45.17, 6.3) * mm});
            skLineSegment(sketch, "E299", {"start": v(-45.17, 6.3) * mm, "end": v(-45.17, 9.8) * mm});
            skLineSegment(sketch, "E300", {"start": v(-45.17, 9.8) * mm, "end": v(-45.17, 12.98) * mm});
            skLineSegment(sketch, "E301", {"start": v(-45.17, 12.98) * mm, "end": v(-45.17, 15.72) * mm});
            skLineSegment(sketch, "E302", {"start": v(-45.17, 15.72) * mm, "end": v(-45.17, 17.91) * mm});
            skLineSegment(sketch, "E303", {"start": v(-45.17, 17.91) * mm, "end": v(-45.17, 19.45) * mm});
            skLineSegment(sketch, "E304", {"start": v(-45.17, 19.45) * mm, "end": v(-45.17, 20.22) * mm});
            skLineSegment(sketch, "E305", {"start": v(-45.17, 20.22) * mm, "end": v(-45.18, 20.82) * mm});
            skLineSegment(sketch, "E306", {"start": v(-45.18, 20.82) * mm, "end": v(-45.21, 21.28) * mm});
            skLineSegment(sketch, "E307", {"start": v(-45.21, 21.28) * mm, "end": v(-45.29, 21.6) * mm});
            skLineSegment(sketch, "E308", {"start": v(-45.29, 21.6) * mm, "end": v(-45.43, 21.83) * mm});
            skLineSegment(sketch, "E309", {"start": v(-45.43, 21.83) * mm, "end": v(-45.66, 21.96) * mm});
            skLineSegment(sketch, "E310", {"start": v(-45.66, 21.96) * mm, "end": v(-46, 22.03) * mm});
            skLineSegment(sketch, "E311", {"start": v(-46, 22.03) * mm, "end": v(-46.46, 22.05) * mm});
            skLineSegment(sketch, "E312", {"start": v(-46.46, 22.05) * mm, "end": v(-47.07, 22.06) * mm});
            skLineSegment(sketch, "E313", {"start": v(-47.07, 22.06) * mm, "end": v(-48.77, 22.06) * mm});
            skLineSegment(sketch, "E314", {"start": v(-48.77, 22.06) * mm, "end": v(-50.81, 22.06) * mm});
            skLineSegment(sketch, "E315", {"start": v(-50.81, 22.06) * mm, "end": v(-52.85, 22.06) * mm});
            skLineSegment(sketch, "E316", {"start": v(-52.85, 22.06) * mm, "end": v(-54.54, 22.06) * mm});
            skLineSegment(sketch, "E317", {"start": v(-54.54, 22.06) * mm, "end": v(-55.23, 22.14) * mm});
            skLineSegment(sketch, "E318", {"start": v(-55.23, 22.14) * mm, "end": v(-55.9, 22.38) * mm});
            skLineSegment(sketch, "E319", {"start": v(-55.9, 22.38) * mm, "end": v(-56.53, 22.74) * mm});
            skLineSegment(sketch, "E320", {"start": v(-56.53, 22.74) * mm, "end": v(-57.1, 23.22) * mm});
            skLineSegment(sketch, "E321", {"start": v(-57.1, 23.22) * mm, "end": v(-57.56, 23.79) * mm});
            skLineSegment(sketch, "E322", {"start": v(-57.56, 23.79) * mm, "end": v(-57.93, 24.42) * mm});
            skLineSegment(sketch, "E323", {"start": v(-57.93, 24.42) * mm, "end": v(-58.16, 25.1) * mm});
            skLineSegment(sketch, "E324", {"start": v(-58.16, 25.1) * mm, "end": v(-58.24, 25.79) * mm});
            skLineSegment(sketch, "E325", {"start": v(-58.24, 25.79) * mm, "end": v(-58.16, 26.49) * mm});
            skLineSegment(sketch, "E326", {"start": v(-58.16, 26.49) * mm, "end": v(-57.93, 27.16) * mm});
            skLineSegment(sketch, "E327", {"start": v(-57.93, 27.16) * mm, "end": v(-57.56, 27.79) * mm});
            skLineSegment(sketch, "E328", {"start": v(-57.56, 27.79) * mm, "end": v(-57.1, 28.35) * mm});
            skLineSegment(sketch, "E329", {"start": v(-57.1, 28.35) * mm, "end": v(-56.53, 28.83) * mm});
            skLineSegment(sketch, "E330", {"start": v(-56.53, 28.83) * mm, "end": v(-55.9, 29.2) * mm});
            skLineSegment(sketch, "E331", {"start": v(-55.9, 29.2) * mm, "end": v(-55.23, 29.43) * mm});
            skLineSegment(sketch, "E332", {"start": v(-55.23, 29.43) * mm, "end": v(-54.54, 29.52) * mm});
            skLineSegment(sketch, "E333", {"start": v(-54.54, 29.52) * mm, "end": v(-53.83, 29.52) * mm});
            skLineSegment(sketch, "E334", {"start": v(-53.83, 29.52) * mm, "end": v(-52.35, 29.52) * mm});
            skLineSegment(sketch, "E335", {"start": v(-52.35, 29.52) * mm, "end": v(-50.19, 29.52) * mm});
            skLineSegment(sketch, "E336", {"start": v(-50.19, 29.52) * mm, "end": v(-47.47, 29.52) * mm});
            skLineSegment(sketch, "E337", {"start": v(-47.47, 29.52) * mm, "end": v(-44.3, 29.52) * mm});
            skLineSegment(sketch, "E338", {"start": v(-44.3, 29.52) * mm, "end": v(-40.8, 29.52) * mm});
            skLineSegment(sketch, "E339", {"start": v(-40.8, 29.52) * mm, "end": v(-37.06, 29.52) * mm});
            skLineSegment(sketch, "E340", {"start": v(-37.06, 29.52) * mm, "end": v(-33.2, 29.52) * mm});
            skLineSegment(sketch, "E341", {"start": v(-33.2, 29.52) * mm, "end": v(-29.35, 29.52) * mm});
            skLineSegment(sketch, "E342", {"start": v(-29.35, 29.52) * mm, "end": v(-25.6, 29.52) * mm});
            skLineSegment(sketch, "E343", {"start": v(-25.6, 29.52) * mm, "end": v(-22.07, 29.52) * mm});
            skLineSegment(sketch, "E344", {"start": v(-22.07, 29.52) * mm, "end": v(-18.87, 29.52) * mm});
            skLineSegment(sketch, "E345", {"start": v(-18.87, 29.52) * mm, "end": v(-16.1, 29.52) * mm});
            skLineSegment(sketch, "E346", {"start": v(-16.1, 29.52) * mm, "end": v(-13.9, 29.52) * mm});
            skLineSegment(sketch, "E347", {"start": v(-13.9, 29.52) * mm, "end": v(-12.35, 29.52) * mm});
            skLineSegment(sketch, "E348", {"start": v(-12.35, 29.52) * mm, "end": v(-11.57, 29.52) * mm});
            skLineSegment(sketch, "E349", {"start": v(-11.57, 29.52) * mm, "end": v(-10.96, 29.52) * mm});
            skLineSegment(sketch, "E350", {"start": v(-10.96, 29.52) * mm, "end": v(-10.5, 29.55) * mm});
            skLineSegment(sketch, "E351", {"start": v(-10.5, 29.55) * mm, "end": v(-10.16, 29.62) * mm});
            skLineSegment(sketch, "E352", {"start": v(-10.16, 29.62) * mm, "end": v(-9.93, 29.75) * mm});
            skLineSegment(sketch, "E353", {"start": v(-9.93, 29.75) * mm, "end": v(-9.79, 29.98) * mm});
            skLineSegment(sketch, "E354", {"start": v(-9.79, 29.98) * mm, "end": v(-9.71, 30.32) * mm});
            skLineSegment(sketch, "E355", {"start": v(-9.71, 30.32) * mm, "end": v(-9.69, 30.79) * mm});
            skLineSegment(sketch, "E356", {"start": v(-9.69, 30.79) * mm, "end": v(-9.68, 31.41) * mm});
            skLineSegment(sketch, "E357", {"start": v(-9.68, 31.41) * mm, "end": v(-9.68, 32.43) * mm});
            skLineSegment(sketch, "E358", {"start": v(-9.68, 32.43) * mm, "end": v(-9.68, 33.98) * mm});
            skLineSegment(sketch, "E359", {"start": v(-9.68, 33.98) * mm, "end": v(-9.68, 35.87) * mm});
            skLineSegment(sketch, "E360", {"start": v(-9.68, 35.87) * mm, "end": v(-9.68, 37.94) * mm});
            skLineSegment(sketch, "E361", {"start": v(-9.68, 37.94) * mm, "end": v(-9.68, 40.02) * mm});
            skLineSegment(sketch, "E362", {"start": v(-9.68, 40.02) * mm, "end": v(-9.68, 41.91) * mm});
            skLineSegment(sketch, "E363", {"start": v(-9.68, 41.91) * mm, "end": v(-9.68, 43.46) * mm});
            skLineSegment(sketch, "E364", {"start": v(-9.68, 43.46) * mm, "end": v(-9.68, 44.48) * mm});
            skLineSegment(sketch, "E365", {"start": v(-9.68, 44.48) * mm, "end": v(-9.68, 45.09) * mm});
            skLineSegment(sketch, "E366", {"start": v(-9.68, 45.09) * mm, "end": v(-9.71, 45.54) * mm});
            skLineSegment(sketch, "E367", {"start": v(-9.71, 45.54) * mm, "end": v(-9.78, 45.87) * mm});
            skLineSegment(sketch, "E368", {"start": v(-9.78, 45.87) * mm, "end": v(-9.92, 46.09) * mm});
            skLineSegment(sketch, "E369", {"start": v(-9.92, 46.09) * mm, "end": v(-10.14, 46.22) * mm});
            skLineSegment(sketch, "E370", {"start": v(-10.14, 46.22) * mm, "end": v(-10.48, 46.29) * mm});
            skLineSegment(sketch, "E371", {"start": v(-10.48, 46.29) * mm, "end": v(-10.95, 46.31) * mm});
            skLineSegment(sketch, "E372", {"start": v(-10.95, 46.31) * mm, "end": v(-11.57, 46.32) * mm});
            skLineSegment(sketch, "E373", {"start": v(-11.57, 46.32) * mm, "end": v(-12.83, 46.32) * mm});
            skLineSegment(sketch, "E374", {"start": v(-12.83, 46.32) * mm, "end": v(-15, 46.32) * mm});
            skLineSegment(sketch, "E375", {"start": v(-15, 46.32) * mm, "end": v(-17.8, 46.32) * mm});
            skLineSegment(sketch, "E376", {"start": v(-17.8, 46.32) * mm, "end": v(-20.9, 46.32) * mm});
            skLineSegment(sketch, "E377", {"start": v(-20.9, 46.32) * mm, "end": v(-24, 46.32) * mm});
            skLineSegment(sketch, "E378", {"start": v(-24, 46.32) * mm, "end": v(-26.8, 46.32) * mm});
            skLineSegment(sketch, "E379", {"start": v(-26.8, 46.32) * mm, "end": v(-29, 46.32) * mm});
            skLineSegment(sketch, "E380", {"start": v(-29, 46.32) * mm, "end": v(-30.25, 46.32) * mm});
            skLineSegment(sketch, "E381", {"start": v(20.2, -24.6) * mm, "end": v(21.1, -24.6) * mm});
            skLineSegment(sketch, "E382", {"start": v(21.1, -24.6) * mm, "end": v(22.4, -24.55) * mm});
            skLineSegment(sketch, "E383", {"start": v(22.4, -24.55) * mm, "end": v(24, -24.43) * mm});
            skLineSegment(sketch, "E384", {"start": v(24, -24.43) * mm, "end": v(25.86, -24.2) * mm});
            skLineSegment(sketch, "E385", {"start": v(25.86, -24.2) * mm, "end": v(27.92, -23.8) * mm});
            skLineSegment(sketch, "E386", {"start": v(27.92, -23.8) * mm, "end": v(30.11, -23.23) * mm});
            skLineSegment(sketch, "E387", {"start": v(30.11, -23.23) * mm, "end": v(32.39, -22.42) * mm});
            skLineSegment(sketch, "E388", {"start": v(32.39, -22.42) * mm, "end": v(34.68, -21.34) * mm});
            skLineSegment(sketch, "E389", {"start": v(34.68, -21.34) * mm, "end": v(36.93, -19.95) * mm});
            skLineSegment(sketch, "E390", {"start": v(36.93, -19.95) * mm, "end": v(39.07, -18.23) * mm});
            skLineSegment(sketch, "E391", {"start": v(39.07, -18.23) * mm, "end": v(41.05, -16.11) * mm});
            skLineSegment(sketch, "E392", {"start": v(41.05, -16.11) * mm, "end": v(42.8, -13.58) * mm});
            skLineSegment(sketch, "E393", {"start": v(42.8, -13.58) * mm, "end": v(44.27, -10.59) * mm});
            skLineSegment(sketch, "E394", {"start": v(44.27, -10.59) * mm, "end": v(45.39, -7.1) * mm});
            skLineSegment(sketch, "E395", {"start": v(46.1, -3.07) * mm, "end": v(46.35, 1.52) * mm});
            skLineSegment(sketch, "E396", {"start": v(46.35, 1.52) * mm, "end": v(46.07, 5.14) * mm});
            skLineSegment(sketch, "E397", {"start": v(46.07, 5.14) * mm, "end": v(45.3, 8.3) * mm});
            skLineSegment(sketch, "E398", {"start": v(45.3, 8.3) * mm, "end": v(44.08, 11.04) * mm});
            skLineSegment(sketch, "E399", {"start": v(44.08, 11.04) * mm, "end": v(42.51, 13.4) * mm});
            skLineSegment(sketch, "E400", {"start": v(42.51, 13.4) * mm, "end": v(40.64, 15.39) * mm});
            skLineSegment(sketch, "E401", {"start": v(40.64, 15.39) * mm, "end": v(38.55, 17.05) * mm});
            skLineSegment(sketch, "E402", {"start": v(38.55, 17.05) * mm, "end": v(36.3, 18.4) * mm});
            skLineSegment(sketch, "E403", {"start": v(36.3, 18.4) * mm, "end": v(33.96, 19.5) * mm});
            skLineSegment(sketch, "E404", {"start": v(33.96, 19.5) * mm, "end": v(31.6, 20.34) * mm});
            skLineSegment(sketch, "E405", {"start": v(31.6, 20.34) * mm, "end": v(29.28, 20.97) * mm});
            skLineSegment(sketch, "E406", {"start": v(29.28, 20.97) * mm, "end": v(27.08, 21.43) * mm});
            skLineSegment(sketch, "E407", {"start": v(27.08, 21.43) * mm, "end": v(25.06, 21.74) * mm});
            skLineSegment(sketch, "E408", {"start": v(25.06, 21.74) * mm, "end": v(23.3, 21.92) * mm});
            skLineSegment(sketch, "E409", {"start": v(23.3, 21.92) * mm, "end": v(21.85, 22.02) * mm});
            skLineSegment(sketch, "E410", {"start": v(21.85, 22.02) * mm, "end": v(20.8, 22.05) * mm});
            skLineSegment(sketch, "E411", {"start": v(20.8, 22.05) * mm, "end": v(20.2, 22.06) * mm});
            skLineSegment(sketch, "E412", {"start": v(20.2, 22.06) * mm, "end": v(18.85, 22.06) * mm});
            skLineSegment(sketch, "E413", {"start": v(18.85, 22.06) * mm, "end": v(16.45, 22.06) * mm});
            skLineSegment(sketch, "E414", {"start": v(16.45, 22.06) * mm, "end": v(13.35, 22.06) * mm});
            skLineSegment(sketch, "E415", {"start": v(13.35, 22.06) * mm, "end": v(9.9, 22.06) * mm});
            skLineSegment(sketch, "E416", {"start": v(9.9, 22.06) * mm, "end": v(6.46, 22.06) * mm});
            skLineSegment(sketch, "E417", {"start": v(6.46, 22.06) * mm, "end": v(3.37, 22.06) * mm});
            skLineSegment(sketch, "E418", {"start": v(3.37, 22.06) * mm, "end": v(0.97, 22.06) * mm});
            skLineSegment(sketch, "E419", {"start": v(0.97, 22.06) * mm, "end": v(-0.37, 22.06) * mm});
            skLineSegment(sketch, "E420", {"start": v(-0.37, 22.06) * mm, "end": v(-0.98, 22.05) * mm});
            skLineSegment(sketch, "E421", {"start": v(-0.98, 22.05) * mm, "end": v(-1.43, 22.03) * mm});
            skLineSegment(sketch, "E422", {"start": v(-1.43, 22.03) * mm, "end": v(-1.76, 21.96) * mm});
            skLineSegment(sketch, "E423", {"start": v(-1.76, 21.96) * mm, "end": v(-1.98, 21.83) * mm});
            skLineSegment(sketch, "E424", {"start": v(-1.98, 21.83) * mm, "end": v(-2.11, 21.6) * mm});
            skLineSegment(sketch, "E425", {"start": v(-2.11, 21.6) * mm, "end": v(-2.18, 21.28) * mm});
            skLineSegment(sketch, "E426", {"start": v(-2.18, 21.28) * mm, "end": v(-2.2, 20.83) * mm});
            skLineSegment(sketch, "E427", {"start": v(-2.2, 20.83) * mm, "end": v(-2.21, 20.22) * mm});
            skLineSegment(sketch, "E428", {"start": v(-2.21, 20.22) * mm, "end": v(-2.21, 19.2) * mm});
            skLineSegment(sketch, "E429", {"start": v(-2.21, 19.2) * mm, "end": v(-2.21, 17.65) * mm});
            skLineSegment(sketch, "E430", {"start": v(-2.21, 17.65) * mm, "end": v(-2.21, 15.75) * mm});
            skLineSegment(sketch, "E431", {"start": v(-2.21, 15.75) * mm, "end": v(-2.21, 13.69) * mm});
            skLineSegment(sketch, "E432", {"start": v(-2.21, 13.69) * mm, "end": v(-2.21, 11.61) * mm});
            skLineSegment(sketch, "E433", {"start": v(-2.21, 11.61) * mm, "end": v(-2.21, 9.72) * mm});
            skLineSegment(sketch, "E434", {"start": v(-2.21, 9.72) * mm, "end": v(-2.21, 8.17) * mm});
            skLineSegment(sketch, "E435", {"start": v(-2.21, 8.17) * mm, "end": v(-2.21, 7.15) * mm});
            skLineSegment(sketch, "E436", {"start": v(-2.21, 7.15) * mm, "end": v(-2.2, 6.53) * mm});
            skLineSegment(sketch, "E437", {"start": v(-2.2, 6.53) * mm, "end": v(-2.18, 6.06) * mm});
            skLineSegment(sketch, "E438", {"start": v(-2.18, 6.06) * mm, "end": v(-2.11, 5.72) * mm});
            skLineSegment(sketch, "E439", {"start": v(-2.11, 5.72) * mm, "end": v(-1.98, 5.5) * mm});
            skLineSegment(sketch, "E440", {"start": v(-1.98, 5.5) * mm, "end": v(-1.76, 5.36) * mm});
            skLineSegment(sketch, "E441", {"start": v(-1.76, 5.36) * mm, "end": v(-1.43, 5.29) * mm});
            skLineSegment(sketch, "E442", {"start": v(-1.43, 5.29) * mm, "end": v(-0.98, 5.26) * mm});
            skLineSegment(sketch, "E443", {"start": v(-0.98, 5.26) * mm, "end": v(-0.37, 5.26) * mm});
            skLineSegment(sketch, "E444", {"start": v(-0.37, 5.26) * mm, "end": v(0.46, 5.26) * mm});
            skLineSegment(sketch, "E445", {"start": v(0.46, 5.26) * mm, "end": v(1.74, 5.26) * mm});
            skLineSegment(sketch, "E446", {"start": v(1.74, 5.26) * mm, "end": v(3.33, 5.26) * mm});
            skLineSegment(sketch, "E447", {"start": v(3.33, 5.26) * mm, "end": v(5.08, 5.26) * mm});
            skLineSegment(sketch, "E448", {"start": v(5.08, 5.26) * mm, "end": v(6.86, 5.26) * mm});
            skLineSegment(sketch, "E449", {"start": v(6.86, 5.26) * mm, "end": v(8.5, 5.26) * mm});
            skLineSegment(sketch, "E450", {"start": v(8.5, 5.26) * mm, "end": v(9.88, 5.26) * mm});
            skLineSegment(sketch, "E451", {"start": v(9.88, 5.26) * mm, "end": v(10.83, 5.26) * mm});
            skLineSegment(sketch, "E452", {"start": v(10.83, 5.26) * mm, "end": v(11.46, 5.26) * mm});
            skLineSegment(sketch, "E453", {"start": v(11.46, 5.26) * mm, "end": v(11.93, 5.29) * mm});
            skLineSegment(sketch, "E454", {"start": v(11.93, 5.29) * mm, "end": v(12.27, 5.36) * mm});
            skLineSegment(sketch, "E455", {"start": v(12.27, 5.36) * mm, "end": v(12.5, 5.5) * mm});
            skLineSegment(sketch, "E456", {"start": v(12.5, 5.5) * mm, "end": v(12.63, 5.72) * mm});
            skLineSegment(sketch, "E457", {"start": v(12.63, 5.72) * mm, "end": v(12.7, 6.06) * mm});
            skLineSegment(sketch, "E458", {"start": v(12.7, 6.06) * mm, "end": v(12.73, 6.53) * mm});
            skLineSegment(sketch, "E459", {"start": v(12.73, 6.53) * mm, "end": v(12.73, 7.15) * mm});
            skLineSegment(sketch, "E460", {"start": v(12.73, 7.15) * mm, "end": v(12.73, 9.84) * mm});
            skLineSegment(sketch, "E461", {"start": v(12.73, 9.84) * mm, "end": v(12.73, 12.75) * mm});
            skLineSegment(sketch, "E462", {"start": v(12.73, 12.75) * mm, "end": v(12.81, 13.44) * mm});
            skLineSegment(sketch, "E463", {"start": v(12.81, 13.44) * mm, "end": v(13.05, 14.12) * mm});
            skLineSegment(sketch, "E464", {"start": v(13.05, 14.12) * mm, "end": v(13.42, 14.74) * mm});
            skLineSegment(sketch, "E465", {"start": v(13.42, 14.74) * mm, "end": v(13.9, 15.3) * mm});
            skLineSegment(sketch, "E466", {"start": v(13.9, 15.3) * mm, "end": v(14.46, 15.78) * mm});
            skLineSegment(sketch, "E467", {"start": v(14.46, 15.78) * mm, "end": v(15.1, 16.14) * mm});
            skLineSegment(sketch, "E468", {"start": v(15.1, 16.14) * mm, "end": v(15.77, 16.37) * mm});
            skLineSegment(sketch, "E469", {"start": v(15.77, 16.37) * mm, "end": v(16.47, 16.46) * mm});
            skLineSegment(sketch, "E470", {"start": v(16.47, 16.46) * mm, "end": v(17.16, 16.37) * mm});
            skLineSegment(sketch, "E471", {"start": v(17.16, 16.37) * mm, "end": v(17.84, 16.14) * mm});
            skLineSegment(sketch, "E472", {"start": v(17.84, 16.14) * mm, "end": v(18.47, 15.78) * mm});
            skLineSegment(sketch, "E473", {"start": v(18.47, 15.78) * mm, "end": v(19.03, 15.3) * mm});
            skLineSegment(sketch, "E474", {"start": v(19.03, 15.3) * mm, "end": v(19.51, 14.74) * mm});
            skLineSegment(sketch, "E475", {"start": v(19.51, 14.74) * mm, "end": v(19.88, 14.12) * mm});
            skLineSegment(sketch, "E476", {"start": v(19.88, 14.12) * mm, "end": v(20.12, 13.44) * mm});
            skLineSegment(sketch, "E477", {"start": v(20.12, 13.44) * mm, "end": v(20.2, 12.75) * mm});
            skLineSegment(sketch, "E478", {"start": v(20.2, 12.75) * mm, "end": v(20.2, 11.37) * mm});
            skLineSegment(sketch, "E479", {"start": v(20.2, 11.37) * mm, "end": v(20.2, 8.88) * mm});
            skLineSegment(sketch, "E480", {"start": v(20.2, 8.88) * mm, "end": v(20.2, 5.63) * mm});
            skLineSegment(sketch, "E481", {"start": v(20.2, 5.63) * mm, "end": v(20.2, 1.97) * mm});
            skLineSegment(sketch, "E482", {"start": v(20.2, 1.97) * mm, "end": v(20.2, -1.75) * mm});
            skLineSegment(sketch, "E483", {"start": v(20.2, -1.75) * mm, "end": v(20.2, -5.16) * mm});
            skLineSegment(sketch, "E484", {"start": v(20.2, -5.16) * mm, "end": v(20.2, -7.92) * mm});
            skLineSegment(sketch, "E485", {"start": v(20.2, -7.92) * mm, "end": v(20.2, -9.67) * mm});
            skLineSegment(sketch, "E486", {"start": v(20.2, -9.67) * mm, "end": v(20.12, -10.53) * mm});
            skLineSegment(sketch, "E487", {"start": v(20.12, -10.53) * mm, "end": v(19.88, -11.28) * mm});
            skLineSegment(sketch, "E488", {"start": v(19.88, -11.28) * mm, "end": v(19.51, -11.92) * mm});
            skLineSegment(sketch, "E489", {"start": v(19.51, -11.92) * mm, "end": v(19.03, -12.45) * mm});
            skLineSegment(sketch, "E490", {"start": v(19.03, -12.45) * mm, "end": v(18.47, -12.87) * mm});
            skLineSegment(sketch, "E491", {"start": v(18.47, -12.87) * mm, "end": v(17.84, -13.16) * mm});
            skLineSegment(sketch, "E492", {"start": v(17.84, -13.16) * mm, "end": v(17.16, -13.35) * mm});
            skLineSegment(sketch, "E493", {"start": v(17.16, -13.35) * mm, "end": v(16.47, -13.4) * mm});
            skLineSegment(sketch, "E494", {"start": v(16.47, -13.4) * mm, "end": v(15.77, -13.32) * mm});
            skLineSegment(sketch, "E495", {"start": v(15.77, -13.32) * mm, "end": v(15.1, -13.08) * mm});
            skLineSegment(sketch, "E496", {"start": v(15.1, -13.08) * mm, "end": v(14.46, -12.7) * mm});
            skLineSegment(sketch, "E497", {"start": v(14.46, -12.7) * mm, "end": v(13.9, -12.23) * mm});
            skLineSegment(sketch, "E498", {"start": v(13.9, -12.23) * mm, "end": v(13.42, -11.66) * mm});
            skLineSegment(sketch, "E499", {"start": v(13.42, -11.66) * mm, "end": v(13.05, -11.03) * mm});
            skLineSegment(sketch, "E500", {"start": v(13.05, -11.03) * mm, "end": v(12.81, -10.36) * mm});
            skLineSegment(sketch, "E501", {"start": v(12.81, -10.36) * mm, "end": v(12.73, -9.67) * mm});
            skLineSegment(sketch, "E502", {"start": v(12.73, -9.67) * mm, "end": v(12.73, -4.05) * mm});
            skLineSegment(sketch, "E503", {"start": v(12.73, -4.05) * mm, "end": v(12.72, -3.44) * mm});
            skLineSegment(sketch, "E504", {"start": v(12.72, -3.44) * mm, "end": v(12.7, -2.99) * mm});
            skLineSegment(sketch, "E505", {"start": v(12.7, -2.99) * mm, "end": v(12.62, -2.66) * mm});
            skLineSegment(sketch, "E506", {"start": v(12.62, -2.66) * mm, "end": v(12.48, -2.44) * mm});
            skLineSegment(sketch, "E507", {"start": v(12.48, -2.44) * mm, "end": v(12.26, -2.3) * mm});
            skLineSegment(sketch, "E508", {"start": v(12.26, -2.3) * mm, "end": v(11.92, -2.24) * mm});
            skLineSegment(sketch, "E509", {"start": v(11.92, -2.24) * mm, "end": v(11.46, -2.21) * mm});
            skLineSegment(sketch, "E510", {"start": v(11.46, -2.21) * mm, "end": v(10.84, -2.21) * mm});
            skLineSegment(sketch, "E511", {"start": v(10.84, -2.21) * mm, "end": v(8.56, -2.21) * mm});
            skLineSegment(sketch, "E512", {"start": v(8.56, -2.21) * mm, "end": v(5.23, -2.21) * mm});
            skLineSegment(sketch, "E513", {"start": v(5.23, -2.21) * mm, "end": v(1.9, -2.21) * mm});
            skLineSegment(sketch, "E514", {"start": v(1.9, -2.21) * mm, "end": v(-0.37, -2.21) * mm});
            skLineSegment(sketch, "E515", {"start": v(-0.37, -2.21) * mm, "end": v(-0.98, -2.22) * mm});
            skLineSegment(sketch, "E516", {"start": v(-0.98, -2.22) * mm, "end": v(-1.43, -2.27) * mm});
            skLineSegment(sketch, "E517", {"start": v(-1.43, -2.27) * mm, "end": v(-1.76, -2.36) * mm});
            skLineSegment(sketch, "E518", {"start": v(-1.76, -2.36) * mm, "end": v(-1.98, -2.52) * mm});
            skLineSegment(sketch, "E519", {"start": v(-1.98, -2.52) * mm, "end": v(-2.11, -2.75) * mm});
            skLineSegment(sketch, "E520", {"start": v(-2.11, -2.75) * mm, "end": v(-2.18, -3.07) * mm});
            skLineSegment(sketch, "E521", {"start": v(-2.18, -3.07) * mm, "end": v(-2.2, -3.5) * mm});
            skLineSegment(sketch, "E522", {"start": v(-2.2, -3.5) * mm, "end": v(-2.21, -4.05) * mm});
            skLineSegment(sketch, "E523", {"start": v(-2.21, -4.05) * mm, "end": v(-2.21, -5.3) * mm});
            skLineSegment(sketch, "E524", {"start": v(-2.21, -5.3) * mm, "end": v(-2.21, -7.49) * mm});
            skLineSegment(sketch, "E525", {"start": v(-2.21, -7.49) * mm, "end": v(-2.21, -10.28) * mm});
            skLineSegment(sketch, "E526", {"start": v(-2.21, -10.28) * mm, "end": v(-2.21, -13.38) * mm});
            skLineSegment(sketch, "E527", {"start": v(-2.21, -13.38) * mm, "end": v(-2.21, -16.48) * mm});
            skLineSegment(sketch, "E528", {"start": v(-2.21, -16.48) * mm, "end": v(-2.21, -19.27) * mm});
            skLineSegment(sketch, "E529", {"start": v(-2.21, -19.27) * mm, "end": v(-2.21, -21.45) * mm});
            skLineSegment(sketch, "E530", {"start": v(-2.21, -21.45) * mm, "end": v(-2.21, -22.71) * mm});
            skLineSegment(sketch, "E531", {"start": v(-2.21, -22.71) * mm, "end": v(-2.2, -23.34) * mm});
            skLineSegment(sketch, "E532", {"start": v(-2.2, -23.34) * mm, "end": v(-2.18, -23.8) * mm});
            skLineSegment(sketch, "E533", {"start": v(-2.18, -23.8) * mm, "end": v(-2.11, -24.14) * mm});
            skLineSegment(sketch, "E534", {"start": v(-2.11, -24.14) * mm, "end": v(-1.98, -24.37) * mm});
            skLineSegment(sketch, "E535", {"start": v(-1.98, -24.37) * mm, "end": v(-1.76, -24.5) * mm});
            skLineSegment(sketch, "E536", {"start": v(-1.76, -24.5) * mm, "end": v(-1.43, -24.57) * mm});
            skLineSegment(sketch, "E537", {"start": v(-1.43, -24.57) * mm, "end": v(-0.98, -24.6) * mm});
            skLineSegment(sketch, "E538", {"start": v(-0.98, -24.6) * mm, "end": v(-0.37, -24.6) * mm});
            skLineSegment(sketch, "E539", {"start": v(-0.37, -24.6) * mm, "end": v(0.87, -24.6) * mm});
            skLineSegment(sketch, "E540", {"start": v(0.87, -24.6) * mm, "end": v(3, -24.6) * mm});
            skLineSegment(sketch, "E541", {"start": v(3, -24.6) * mm, "end": v(5.79, -24.6) * mm});
            skLineSegment(sketch, "E542", {"start": v(5.79, -24.6) * mm, "end": v(8.95, -24.6) * mm});
            skLineSegment(sketch, "E543", {"start": v(8.95, -24.6) * mm, "end": v(12.23, -24.6) * mm});
            skLineSegment(sketch, "E544", {"start": v(12.23, -24.6) * mm, "end": v(15.37, -24.6) * mm});
            skLineSegment(sketch, "E545", {"start": v(15.37, -24.6) * mm, "end": v(18.12, -24.6) * mm});
            skLineSegment(sketch, "E546", {"start": v(18.12, -24.6) * mm, "end": v(20.2, -24.6) * mm});
            skLineSegment(sketch, "E547", {"start": v(-9.68, -22.7) * mm, "end": v(-9.68, -21.94) * mm});
            skLineSegment(sketch, "E548", {"start": v(-9.68, -21.94) * mm, "end": v(-9.68, -20.4) * mm});
            skLineSegment(sketch, "E549", {"start": v(-9.68, -20.4) * mm, "end": v(-9.68, -18.2) * mm});
            skLineSegment(sketch, "E550", {"start": v(-9.68, -18.2) * mm, "end": v(-9.68, -15.45) * mm});
            skLineSegment(sketch, "E551", {"start": v(-9.68, -15.45) * mm, "end": v(-9.68, -12.26) * mm});
            skLineSegment(sketch, "E552", {"start": v(-9.68, -12.26) * mm, "end": v(-9.68, -8.75) * mm});
            skLineSegment(sketch, "E553", {"start": v(-9.68, -8.75) * mm, "end": v(-9.68, -5.01) * mm});
            skLineSegment(sketch, "E554", {"start": v(-9.68, -5.01) * mm, "end": v(-9.68, -1.17) * mm});
            skLineSegment(sketch, "E555", {"start": v(-9.68, -1.17) * mm, "end": v(-9.68, 2.67) * mm});
            skLineSegment(sketch, "E556", {"start": v(-9.68, 2.67) * mm, "end": v(-9.68, 6.4) * mm});
            skLineSegment(sketch, "E557", {"start": v(-9.68, 6.4) * mm, "end": v(-9.68, 9.9) * mm});
            skLineSegment(sketch, "E558", {"start": v(-9.68, 9.9) * mm, "end": v(-9.68, 13.07) * mm});
            skLineSegment(sketch, "E559", {"start": v(-9.68, 13.07) * mm, "end": v(-9.68, 15.8) * mm});
            skLineSegment(sketch, "E560", {"start": v(-9.68, 15.8) * mm, "end": v(-9.68, 17.97) * mm});
            skLineSegment(sketch, "E561", {"start": v(-9.68, 17.97) * mm, "end": v(-9.68, 19.48) * mm});
            skLineSegment(sketch, "E562", {"start": v(-9.68, 19.48) * mm, "end": v(-9.68, 20.22) * mm});
            skLineSegment(sketch, "E563", {"start": v(-9.68, 20.22) * mm, "end": v(-9.68, 20.83) * mm});
            skLineSegment(sketch, "E564", {"start": v(-9.68, 20.83) * mm, "end": v(-9.71, 21.3) * mm});
            skLineSegment(sketch, "E565", {"start": v(-9.71, 21.3) * mm, "end": v(-9.78, 21.62) * mm});
            skLineSegment(sketch, "E566", {"start": v(-9.78, 21.62) * mm, "end": v(-9.92, 21.84) * mm});
            skLineSegment(sketch, "E567", {"start": v(-9.92, 21.84) * mm, "end": v(-10.14, 21.97) * mm});
            skLineSegment(sketch, "E568", {"start": v(-10.14, 21.97) * mm, "end": v(-10.48, 22.03) * mm});
            skLineSegment(sketch, "E569", {"start": v(-10.48, 22.03) * mm, "end": v(-10.95, 22.05) * mm});
            skLineSegment(sketch, "E570", {"start": v(-10.95, 22.05) * mm, "end": v(-11.58, 22.06) * mm});
            skLineSegment(sketch, "E571", {"start": v(-11.58, 22.06) * mm, "end": v(-13.08, 22.06) * mm});
            skLineSegment(sketch, "E572", {"start": v(-13.08, 22.06) * mm, "end": v(-15.9, 22.06) * mm});
            skLineSegment(sketch, "E573", {"start": v(-15.9, 22.06) * mm, "end": v(-19.59, 22.06) * mm});
            skLineSegment(sketch, "E574", {"start": v(-19.59, 22.06) * mm, "end": v(-23.72, 22.06) * mm});
            skLineSegment(sketch, "E575", {"start": v(-23.72, 22.06) * mm, "end": v(-27.85, 22.06) * mm});
            skLineSegment(sketch, "E576", {"start": v(-27.85, 22.06) * mm, "end": v(-31.54, 22.06) * mm});
            skLineSegment(sketch, "E577", {"start": v(-31.54, 22.06) * mm, "end": v(-34.35, 22.06) * mm});
            skLineSegment(sketch, "E578", {"start": v(-34.35, 22.06) * mm, "end": v(-35.86, 22.06) * mm});
            skLineSegment(sketch, "E579", {"start": v(-35.86, 22.06) * mm, "end": v(-36.46, 22.05) * mm});
            skLineSegment(sketch, "E580", {"start": v(-36.46, 22.05) * mm, "end": v(-36.92, 22.03) * mm});
            skLineSegment(sketch, "E581", {"start": v(-36.92, 22.03) * mm, "end": v(-37.25, 21.96) * mm});
            skLineSegment(sketch, "E582", {"start": v(-37.25, 21.96) * mm, "end": v(-37.47, 21.83) * mm});
            skLineSegment(sketch, "E583", {"start": v(-37.47, 21.83) * mm, "end": v(-37.6, 21.6) * mm});
            skLineSegment(sketch, "E584", {"start": v(-37.6, 21.6) * mm, "end": v(-37.67, 21.28) * mm});
            skLineSegment(sketch, "E585", {"start": v(-37.67, 21.28) * mm, "end": v(-37.7, 20.82) * mm});
            skLineSegment(sketch, "E586", {"start": v(-37.7, 20.82) * mm, "end": v(-37.7, 20.21) * mm});
            skLineSegment(sketch, "E587", {"start": v(-37.7, 20.21) * mm, "end": v(-37.7, 19.48) * mm});
            skLineSegment(sketch, "E588", {"start": v(-37.7, 19.48) * mm, "end": v(-37.7, 17.97) * mm});
            skLineSegment(sketch, "E589", {"start": v(-37.7, 17.97) * mm, "end": v(-37.7, 15.8) * mm});
            skLineSegment(sketch, "E590", {"start": v(-37.7, 15.8) * mm, "end": v(-37.7, 13.07) * mm});
            skLineSegment(sketch, "E591", {"start": v(-37.7, 13.07) * mm, "end": v(-37.7, 9.9) * mm});
            skLineSegment(sketch, "E592", {"start": v(-37.7, 9.9) * mm, "end": v(-37.7, 6.4) * mm});
            skLineSegment(sketch, "E593", {"start": v(-37.7, 6.4) * mm, "end": v(-37.7, 2.68) * mm});
            skLineSegment(sketch, "E594", {"start": v(-37.7, 2.68) * mm, "end": v(-37.7, -1.16) * mm});
            skLineSegment(sketch, "E595", {"start": v(-37.7, -1.16) * mm, "end": v(-37.7, -5) * mm});
            skLineSegment(sketch, "E596", {"start": v(-37.7, -5) * mm, "end": v(-37.7, -8.72) * mm});
            skLineSegment(sketch, "E597", {"start": v(-37.7, -8.72) * mm, "end": v(-37.7, -12.22) * mm});
            skLineSegment(sketch, "E598", {"start": v(-37.7, -12.22) * mm, "end": v(-37.7, -15.4) * mm});
            skLineSegment(sketch, "E599", {"start": v(-37.7, -15.4) * mm, "end": v(-37.7, -18.13) * mm});
            skLineSegment(sketch, "E600", {"start": v(-37.7, -18.13) * mm, "end": v(-37.7, -20.3) * mm});
            skLineSegment(sketch, "E601", {"start": v(-37.7, -20.3) * mm, "end": v(-37.7, -21.83) * mm});
            skLineSegment(sketch, "E602", {"start": v(-37.7, -21.83) * mm, "end": v(-37.7, -22.58) * mm});
            skLineSegment(sketch, "E603", {"start": v(-37.7, -22.58) * mm, "end": v(-37.7, -23.21) * mm});
            skLineSegment(sketch, "E604", {"start": v(-37.7, -23.21) * mm, "end": v(-37.67, -23.7) * mm});
            skLineSegment(sketch, "E605", {"start": v(-37.67, -23.7) * mm, "end": v(-37.6, -24.05) * mm});
            skLineSegment(sketch, "E606", {"start": v(-37.6, -24.05) * mm, "end": v(-37.47, -24.3) * mm});
            skLineSegment(sketch, "E607", {"start": v(-37.47, -24.3) * mm, "end": v(-37.25, -24.46) * mm});
            skLineSegment(sketch, "E608", {"start": v(-37.25, -24.46) * mm, "end": v(-36.92, -24.55) * mm});
            skLineSegment(sketch, "E609", {"start": v(-36.92, -24.55) * mm, "end": v(-36.47, -24.6) * mm});
            skLineSegment(sketch, "E610", {"start": v(-36.47, -24.6) * mm, "end": v(-35.86, -24.6) * mm});
            skLineSegment(sketch, "E611", {"start": v(-35.86, -24.6) * mm, "end": v(-34.36, -24.6) * mm});
            skLineSegment(sketch, "E612", {"start": v(-34.36, -24.6) * mm, "end": v(-31.54, -24.6) * mm});
            skLineSegment(sketch, "E613", {"start": v(-31.54, -24.6) * mm, "end": v(-27.85, -24.6) * mm});
            skLineSegment(sketch, "E614", {"start": v(-27.85, -24.6) * mm, "end": v(-23.72, -24.6) * mm});
            skLineSegment(sketch, "E615", {"start": v(-23.72, -24.6) * mm, "end": v(-19.59, -24.6) * mm});
            skLineSegment(sketch, "E616", {"start": v(-19.59, -24.6) * mm, "end": v(-15.9, -24.6) * mm});
            skLineSegment(sketch, "E617", {"start": v(-15.9, -24.6) * mm, "end": v(-13.08, -24.6) * mm});
            skLineSegment(sketch, "E618", {"start": v(-13.08, -24.6) * mm, "end": v(-11.58, -24.6) * mm});
            skLineSegment(sketch, "E619", {"start": v(-11.58, -24.6) * mm, "end": v(-10.95, -24.6) * mm});
            skLineSegment(sketch, "E620", {"start": v(-10.95, -24.6) * mm, "end": v(-10.48, -24.57) * mm});
            skLineSegment(sketch, "E621", {"start": v(-10.48, -24.57) * mm, "end": v(-10.14, -24.5) * mm});
            skLineSegment(sketch, "E622", {"start": v(-10.14, -24.5) * mm, "end": v(-9.92, -24.37) * mm});
            skLineSegment(sketch, "E623", {"start": v(-9.92, -24.37) * mm, "end": v(-9.78, -24.14) * mm});
            skLineSegment(sketch, "E624", {"start": v(-9.78, -24.14) * mm, "end": v(-9.71, -23.8) * mm});
            skLineSegment(sketch, "E625", {"start": v(-9.71, -23.8) * mm, "end": v(-9.68, -23.33) * mm});
            skLineSegment(sketch, "E626", {"start": v(-9.68, -23.33) * mm, "end": v(-9.68, -22.7) * mm});
            skLineSegment(sketch, "E627", {"start": v(0, 75) * mm, "end": v(7.67, 74.61) * mm});
            skLineSegment(sketch, "E628", {"start": v(7.67, 74.61) * mm, "end": v(15.12, 73.48) * mm});
            skLineSegment(sketch, "E629", {"start": v(15.12, 73.48) * mm, "end": v(22.32, 71.63) * mm});
            skLineSegment(sketch, "E630", {"start": v(22.32, 71.63) * mm, "end": v(29.21, 69.1) * mm});
            skLineSegment(sketch, "E631", {"start": v(29.21, 69.1) * mm, "end": v(35.77, 65.95) * mm});
            skLineSegment(sketch, "E632", {"start": v(35.77, 65.95) * mm, "end": v(41.96, 62.2) * mm});
            skLineSegment(sketch, "E633", {"start": v(41.96, 62.2) * mm, "end": v(47.74, 57.87) * mm});
            skLineSegment(sketch, "E634", {"start": v(47.74, 57.87) * mm, "end": v(53.07, 53.03) * mm});
            skLineSegment(sketch, "E635", {"start": v(53.07, 53.03) * mm, "end": v(57.91, 47.7) * mm});
            skLineSegment(sketch, "E636", {"start": v(57.91, 47.7) * mm, "end": v(62.24, 41.93) * mm});
            skLineSegment(sketch, "E637", {"start": v(62.24, 41.93) * mm, "end": v(66, 35.75) * mm});
            skLineSegment(sketch, "E638", {"start": v(66, 35.75) * mm, "end": v(69.16, 29.2) * mm});
            skLineSegment(sketch, "E639", {"start": v(69.16, 29.2) * mm, "end": v(71.68, 22.3) * mm});
            skLineSegment(sketch, "E640", {"start": v(71.68, 22.3) * mm, "end": v(73.53, 15.12) * mm});
            skLineSegment(sketch, "E641", {"start": v(73.53, 15.12) * mm, "end": v(74.67, 7.67) * mm});
            skLineSegment(sketch, "E642", {"start": v(74.67, 7.67) * mm, "end": v(75.05, 0) * mm});
            skLineSegment(sketch, "E643", {"start": v(75.05, 0) * mm, "end": v(74.67, -7.67) * mm});
            skLineSegment(sketch, "E644", {"start": v(74.67, -7.67) * mm, "end": v(73.53, -15.11) * mm});
            skLineSegment(sketch, "E645", {"start": v(73.53, -15.11) * mm, "end": v(71.68, -22.3) * mm});
            skLineSegment(sketch, "E646", {"start": v(71.68, -22.3) * mm, "end": v(69.16, -29.2) * mm});
            skLineSegment(sketch, "E647", {"start": v(69.16, -29.2) * mm, "end": v(66, -35.75) * mm});
            skLineSegment(sketch, "E648", {"start": v(66, -35.75) * mm, "end": v(62.24, -41.93) * mm});
            skLineSegment(sketch, "E649", {"start": v(62.24, -41.93) * mm, "end": v(57.91, -47.7) * mm});
            skLineSegment(sketch, "E650", {"start": v(57.91, -47.7) * mm, "end": v(53.07, -53.03) * mm});
            skLineSegment(sketch, "E651", {"start": v(53.07, -53.03) * mm, "end": v(47.74, -57.87) * mm});
            skLineSegment(sketch, "E652", {"start": v(47.74, -57.87) * mm, "end": v(41.96, -62.2) * mm});
            skLineSegment(sketch, "E653", {"start": v(41.96, -62.2) * mm, "end": v(35.77, -65.95) * mm});
            skLineSegment(sketch, "E654", {"start": v(35.77, -65.95) * mm, "end": v(29.21, -69.1) * mm});
            skLineSegment(sketch, "E655", {"start": v(29.21, -69.1) * mm, "end": v(22.32, -71.63) * mm});
            skLineSegment(sketch, "E656", {"start": v(22.32, -71.63) * mm, "end": v(15.12, -73.48) * mm});
            skLineSegment(sketch, "E657", {"start": v(15.12, -73.48) * mm, "end": v(7.67, -74.61) * mm});
            skLineSegment(sketch, "E658", {"start": v(7.67, -74.61) * mm, "end": v(0, -75) * mm});
            skLineSegment(sketch, "E659", {"start": v(0, -75) * mm, "end": v(-7.67, -74.61) * mm});
            skLineSegment(sketch, "E660", {"start": v(-7.67, -74.61) * mm, "end": v(-15.13, -73.48) * mm});
            skLineSegment(sketch, "E661", {"start": v(-15.13, -73.48) * mm, "end": v(-22.32, -71.63) * mm});
            skLineSegment(sketch, "E662", {"start": v(-22.32, -71.63) * mm, "end": v(-29.22, -69.1) * mm});
            skLineSegment(sketch, "E663", {"start": v(-29.22, -69.1) * mm, "end": v(-35.78, -65.95) * mm});
            skLineSegment(sketch, "E664", {"start": v(-35.78, -65.95) * mm, "end": v(-41.96, -62.2) * mm});
            skLineSegment(sketch, "E665", {"start": v(-41.96, -62.2) * mm, "end": v(-47.74, -57.87) * mm});
            skLineSegment(sketch, "E666", {"start": v(-47.74, -57.87) * mm, "end": v(-53.07, -53.03) * mm});
            skLineSegment(sketch, "E667", {"start": v(-53.07, -53.03) * mm, "end": v(-57.92, -47.7) * mm});
            skLineSegment(sketch, "E668", {"start": v(-57.92, -47.7) * mm, "end": v(-62.24, -41.93) * mm});
            skLineSegment(sketch, "E669", {"start": v(-62.24, -41.93) * mm, "end": v(-66, -35.75) * mm});
            skLineSegment(sketch, "E670", {"start": v(-66, -35.75) * mm, "end": v(-69.16, -29.2) * mm});
            skLineSegment(sketch, "E671", {"start": v(-69.16, -29.2) * mm, "end": v(-71.68, -22.3) * mm});
            skLineSegment(sketch, "E672", {"start": v(-71.68, -22.3) * mm, "end": v(-73.53, -15.11) * mm});
            skLineSegment(sketch, "E673", {"start": v(-73.53, -15.11) * mm, "end": v(-74.67, -7.67) * mm});
            skLineSegment(sketch, "E674", {"start": v(-74.67, -7.67) * mm, "end": v(-75.05, 0) * mm});
            skLineSegment(sketch, "E675", {"start": v(-75.05, 0) * mm, "end": v(-74.67, 7.67) * mm});
            skLineSegment(sketch, "E676", {"start": v(-74.67, 7.67) * mm, "end": v(-73.53, 15.12) * mm});
            skLineSegment(sketch, "E677", {"start": v(-73.53, 15.12) * mm, "end": v(-71.68, 22.3) * mm});
            skLineSegment(sketch, "E678", {"start": v(-71.68, 22.3) * mm, "end": v(-69.16, 29.2) * mm});
            skLineSegment(sketch, "E679", {"start": v(-69.16, 29.2) * mm, "end": v(-66, 35.75) * mm});
            skLineSegment(sketch, "E680", {"start": v(-66, 35.75) * mm, "end": v(-62.24, 41.93) * mm});
            skLineSegment(sketch, "E681", {"start": v(-62.24, 41.93) * mm, "end": v(-57.92, 47.7) * mm});
            skLineSegment(sketch, "E682", {"start": v(-57.92, 47.7) * mm, "end": v(-53.07, 53.03) * mm});
            skLineSegment(sketch, "E683", {"start": v(-53.07, 53.03) * mm, "end": v(-47.74, 57.87) * mm});
            skLineSegment(sketch, "E684", {"start": v(-47.74, 57.87) * mm, "end": v(-41.96, 62.2) * mm});
            skLineSegment(sketch, "E685", {"start": v(-41.96, 62.2) * mm, "end": v(-35.78, 65.95) * mm});
            skLineSegment(sketch, "E686", {"start": v(-35.78, 65.95) * mm, "end": v(-29.22, 69.1) * mm});
            skLineSegment(sketch, "E687", {"start": v(-29.22, 69.1) * mm, "end": v(-22.32, 71.63) * mm});
            skLineSegment(sketch, "E688", {"start": v(-22.32, 71.63) * mm, "end": v(-15.13, 73.48) * mm});
            skLineSegment(sketch, "E689", {"start": v(-15.13, 73.48) * mm, "end": v(-7.67, 74.61) * mm});
            skLineSegment(sketch, "E690", {"start": v(-7.67, 74.61) * mm, "end": v(0, 75) * mm});
            skPoint(sketch, "E691.middle", {"position": v(0, 0) * mm});
            skPoint(sketch, "E691.right.end.orphan", {"position": v(-80.06, 1) * mm});
            skPoint(sketch, "E691.right.start.orphan", {"position": v(-80.06, -1) * mm});
            skLineSegment(sketch, "E692.trimOffspring", {"start": v(-37.7, 1) * mm, "end": v(-45.17, 1) * mm});
            skLineSegment(sketch, "E693.trimOffspring", {"start": v(-37.7, -1) * mm, "end": v(-45.17, -1) * mm});
            skPoint(sketch, "E694.end.orphan", {"position": v(46.1, -1) * mm});
            skLineSegment(sketch, "E695.trimOffspring", {"start": v(53.8, 1) * mm, "end": v(46.32, 1) * mm});
            skLineSegment(sketch, "E696.trimOffspring", {"start": v(53.69, -1) * mm, "end": v(46.1, -1) * mm});
            skPoint(sketch, "E691.left.end.orphan", {"position": v(80.06, 1) * mm});
            skPoint(sketch, "E691.left.start.orphan", {"position": v(80.06, -1) * mm});
            skLineSegment(sketch, "E697", {"start": v(46.1, -3.07) * mm, "end": v(45.39, -7.1) * mm});
            skSolve(sketch);
        }
        {
            var Q0;
            Q0=makeQuery(id+"F0.imprint","IMPRINT",FACE,{"disambiguationData":[TD([[makeQuery(id+"F0.imprint","IMPRINT",EDGE,{"derivedFrom":sQuery(id+"F0.wireOp",EDGE,"E0")}),1.0]])]});
            var Q1;
            Q1=makeQuery(id+"F0.imprint","IMPRINT",FACE,{"disambiguationData":[TD([[makeQuery(id+"F0.imprint","IMPRINT",EDGE,{"derivedFrom":sQuery(id+"F0.wireOp",EDGE,"E547")}),1.0]])]});
            var Q2;
            Q2=makeQuery(id+"F0.imprint","IMPRINT",FACE,{"disambiguationData":[TD([[makeQuery(id+"F0.imprint","IMPRINT",EDGE,{"derivedFrom":sQuery(id+"F0.wireOp",EDGE,"E381")}),1.0]])]});
            var Q3;
            {var subQ0=sQuery(id+"F0.wireOp",EDGE,"E692.trimOffspring");Q3=makeQuery(id+"F0.imprint","IMPRINT",FACE,{"disambiguationData":[TD([[makeQuery(id+"F0.imprint","IMPRINT",EDGE,{"derivedFrom":subQ0}),1.0]])]});}
            var Q4;
            {var subQ0=sQuery(id+"F0.wireOp",EDGE,"E695.trimOffspring");Q4=makeQuery(id+"F0.imprint","IMPRINT",FACE,{"disambiguationData":[TD([[makeQuery(id+"F0.imprint","IMPRINT",EDGE,{"derivedFrom":subQ0}),1.0]])]});}
            extrude(context, id + "F1", {"entities" : qUnion([Q0, Q1, Q2, Q3, Q4]), "depth" : 1 * mm});
        }
    });
